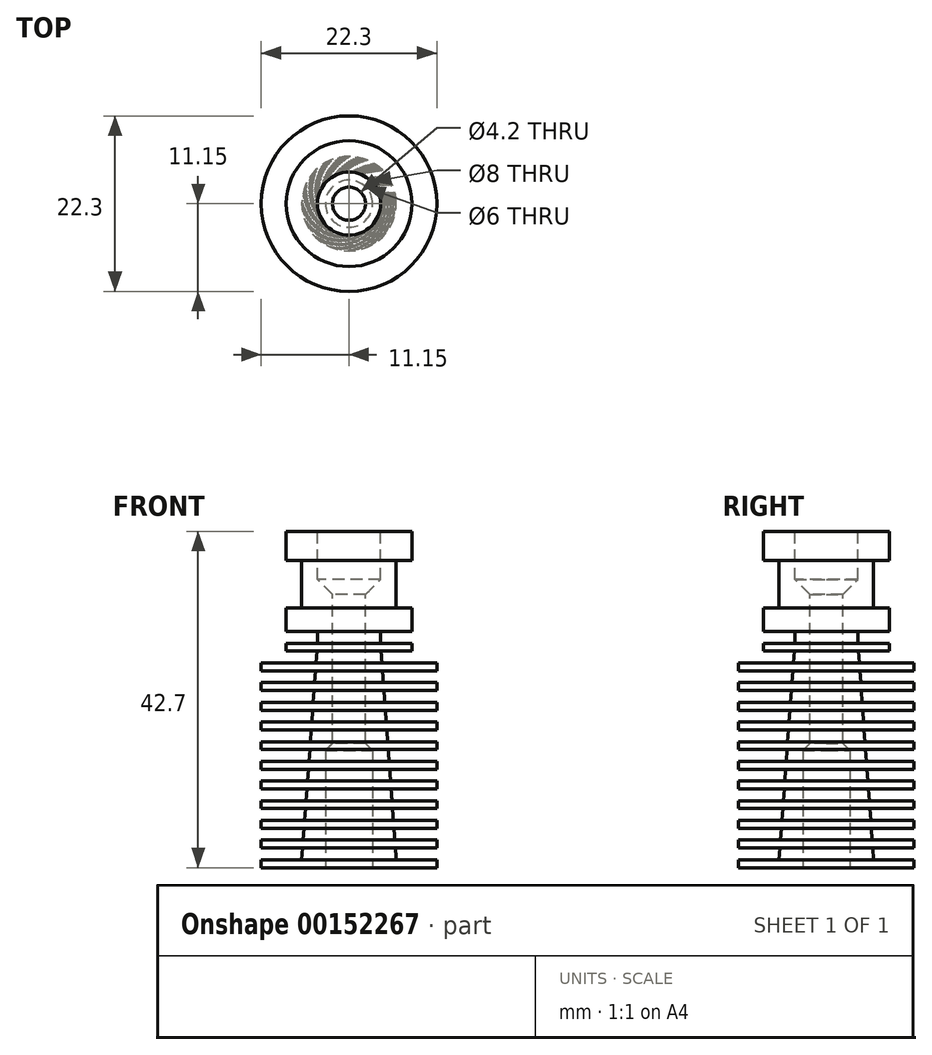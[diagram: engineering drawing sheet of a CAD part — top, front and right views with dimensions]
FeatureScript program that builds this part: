
annotation { "Feature Type Name" : "Feature", "Feature Type Description" : "" }
export const myFeature = defineFeature(function(context is Context, id is Id, definition is map)
    precondition{}
    {
        {
            var Q0;
            Q0=qCreatedBy(makeId("Top.planeOp"),FACE);
            var sketch = newSketch(context, id + "F0", { "sketchPlane" : qUnion([Q0])});
            skCircle(sketch, "E0", {"center": v(0, 0) * mm, "radius": 8 * mm});
            skSolve(sketch);
        }
        {
            var Q0;
            Q0=makeQuery(id+"F0.imprint","IMPRINT",FACE,{"disambiguationData":[TD([[makeQuery(id+"F0.imprint","IMPRINT",EDGE,{"derivedFrom":sQuery(id+"F0.wireOp",EDGE,"E0")}),1.0]])]});
            var Q1;
            Q1=sQuery(id+"F0.wireOp",EDGE,"E0");
            extrude(context, id + "F1", {"entities" : qUnion([Q0]), "surfaceEntities" : qUnion([Q1]), "oppositeDirection" : true, "depth" : 3.7 * mm});
        }
        {
            var Q0;
            Q0=makeQuery(id+"F1.opExtrude","CAP_FACE",FACE,{"disambiguationData":[OSD([sQuery(id+"F0.wireOp",EDGE,"E0")])],"isStart":false});
            var sketch = newSketch(context, id + "F2", { "sketchPlane" : qUnion([Q0])});
            skCircle(sketch, "E1", {"center": v(0, 0) * mm, "radius": 6 * mm});
            skSolve(sketch);
        }
        {
            var Q0;
            Q0=makeQuery(id+"F2.imprint","IMPRINT",FACE,{"disambiguationData":[TD([[makeQuery(id+"F2.imprint","IMPRINT",EDGE,{"derivedFrom":sQuery(id+"F2.wireOp",EDGE,"E1")}),1.0]])]});
            var Q1;
            Q1=sQuery(id+"F2.wireOp",EDGE,"E1");
            extrude(context, id + "F3", {"entities" : qUnion([Q0]), "operationType" : NewBodyOperationType.ADD, "surfaceEntities" : qUnion([Q1]), "depth" : 6 * mm});
        }
        {
            var Q0;
            Q0=makeQuery(id+"F3.opExtrude","CAP_FACE",FACE,{"disambiguationData":[OSD([sQuery(id+"F2.wireOp",EDGE,"E1")])],"isStart":false});
            var sketch = newSketch(context, id + "F4", { "sketchPlane" : qUnion([Q0])});
            skCircle(sketch, "E2", {"center": v(0, 0) * mm, "radius": 8 * mm});
            skSolve(sketch);
        }
        {
            var Q0;
            Q0 = qSketchRegion(id + "F4", true);
            extrude(context, id + "F5", {"entities" : qUnion([Q0]), "operationType" : NewBodyOperationType.ADD, "depth" : 3 * mm});
        }
        {
            var Q0;
            Q0=qCreatedBy(makeId("Front.planeOp"),FACE);
            var sketch = newSketch(context, id + "F6", { "sketchPlane" : qUnion([Q0])});
            skLineSegment(sketch, "E3", {"start": v(0, 0) * mm, "end": v(0, -12.7) * mm});
            skLineSegment(sketch, "E4.bottom", {"start": v(0, -12.7) * mm, "end": v(4, -12.7) * mm});
            skLineSegment(sketch, "E4.top", {"start": v(0, -14.2) * mm, "end": v(4, -14.2) * mm});
            skLineSegment(sketch, "E4.left", {"start": v(0, -12.7) * mm, "end": v(0, -14.2) * mm});
            skLineSegment(sketch, "E4.right", {"start": v(4, -12.7) * mm, "end": v(4, -14.2) * mm});
            skLineSegment(sketch, "E5.bottom", {"start": v(0, -14.2) * mm, "end": v(8, -14.2) * mm});
            skLineSegment(sketch, "E5.top", {"start": v(0, -15.2) * mm, "end": v(8, -15.2) * mm});
            skLineSegment(sketch, "E5.left", {"start": v(0, -14.2) * mm, "end": v(0, -15.2) * mm});
            skLineSegment(sketch, "E5.right", {"start": v(8, -14.2) * mm, "end": v(8, -15.2) * mm});
            skLineSegment(sketch, "E6", {"start": v(0, -15.2) * mm, "end": v(0, -16.7) * mm});
            skLineSegment(sketch, "E7.bottom", {"start": v(0, -16.7) * mm, "end": v(11.15, -16.7) * mm});
            skLineSegment(sketch, "E7.top", {"start": v(0, -17.7) * mm, "end": v(11.15, -17.7) * mm});
            skLineSegment(sketch, "E7.left", {"start": v(0, -16.7) * mm, "end": v(0, -17.7) * mm});
            skLineSegment(sketch, "E7.right", {"start": v(11.15, -16.7) * mm, "end": v(11.15, -17.7) * mm});
            skLineSegment(sketch, "E8.1.0.0", {"start": v(0, -20.2) * mm, "end": v(11.15, -20.2) * mm});
            skLineSegment(sketch, "E8.1.0.1", {"start": v(0, -19.2) * mm, "end": v(11.15, -19.2) * mm});
            skLineSegment(sketch, "E8.1.0.2", {"start": v(0, -19.2) * mm, "end": v(0, -20.2) * mm});
            skLineSegment(sketch, "E8.1.0.3", {"start": v(11.15, -19.2) * mm, "end": v(11.15, -20.2) * mm});
            skLineSegment(sketch, "E8.2.0.0", {"start": v(0, -22.7) * mm, "end": v(11.15, -22.7) * mm});
            skLineSegment(sketch, "E8.2.0.1", {"start": v(0, -21.7) * mm, "end": v(11.15, -21.7) * mm});
            skLineSegment(sketch, "E8.2.0.2", {"start": v(0, -21.7) * mm, "end": v(0, -22.7) * mm});
            skLineSegment(sketch, "E8.2.0.3", {"start": v(11.15, -21.7) * mm, "end": v(11.15, -22.7) * mm});
            skLineSegment(sketch, "E8.3.0.0", {"start": v(0, -25.2) * mm, "end": v(11.15, -25.2) * mm});
            skLineSegment(sketch, "E8.3.0.1", {"start": v(0, -24.2) * mm, "end": v(11.15, -24.2) * mm});
            skLineSegment(sketch, "E8.3.0.2", {"start": v(0, -24.2) * mm, "end": v(0, -25.2) * mm});
            skLineSegment(sketch, "E8.3.0.3", {"start": v(11.15, -24.2) * mm, "end": v(11.15, -25.2) * mm});
            skLineSegment(sketch, "E8.4.0.0", {"start": v(0, -27.7) * mm, "end": v(11.15, -27.7) * mm});
            skLineSegment(sketch, "E8.4.0.1", {"start": v(0, -26.7) * mm, "end": v(11.15, -26.7) * mm});
            skLineSegment(sketch, "E8.4.0.2", {"start": v(0, -26.7) * mm, "end": v(0, -27.7) * mm});
            skLineSegment(sketch, "E8.4.0.3", {"start": v(11.15, -26.7) * mm, "end": v(11.15, -27.7) * mm});
            skLineSegment(sketch, "E8.5.0.0", {"start": v(0, -30.2) * mm, "end": v(11.15, -30.2) * mm});
            skLineSegment(sketch, "E8.5.0.1", {"start": v(0, -29.2) * mm, "end": v(11.15, -29.2) * mm});
            skLineSegment(sketch, "E8.5.0.2", {"start": v(0, -29.2) * mm, "end": v(0, -30.2) * mm});
            skLineSegment(sketch, "E8.5.0.3", {"start": v(11.15, -29.2) * mm, "end": v(11.15, -30.2) * mm});
            skLineSegment(sketch, "E8.6.0.0", {"start": v(0, -32.7) * mm, "end": v(11.15, -32.7) * mm});
            skLineSegment(sketch, "E8.6.0.1", {"start": v(0, -31.7) * mm, "end": v(11.15, -31.7) * mm});
            skLineSegment(sketch, "E8.6.0.2", {"start": v(0, -31.7) * mm, "end": v(0, -32.7) * mm});
            skLineSegment(sketch, "E8.6.0.3", {"start": v(11.15, -31.7) * mm, "end": v(11.15, -32.7) * mm});
            skLineSegment(sketch, "E8.7.0.0", {"start": v(0, -35.2) * mm, "end": v(11.15, -35.2) * mm});
            skLineSegment(sketch, "E8.7.0.1", {"start": v(0, -34.2) * mm, "end": v(11.15, -34.2) * mm});
            skLineSegment(sketch, "E8.7.0.2", {"start": v(0, -34.2) * mm, "end": v(0, -35.2) * mm});
            skLineSegment(sketch, "E8.7.0.3", {"start": v(11.15, -34.2) * mm, "end": v(11.15, -35.2) * mm});
            skLineSegment(sketch, "E8.8.0.0", {"start": v(0, -37.7) * mm, "end": v(11.15, -37.7) * mm});
            skLineSegment(sketch, "E8.8.0.1", {"start": v(0, -36.7) * mm, "end": v(11.15, -36.7) * mm});
            skLineSegment(sketch, "E8.8.0.2", {"start": v(0, -36.7) * mm, "end": v(0, -37.7) * mm});
            skLineSegment(sketch, "E8.8.0.3", {"start": v(11.15, -36.7) * mm, "end": v(11.15, -37.7) * mm});
            skLineSegment(sketch, "E8.9.0.0", {"start": v(0, -40.2) * mm, "end": v(11.15, -40.2) * mm});
            skLineSegment(sketch, "E8.9.0.1", {"start": v(0, -39.2) * mm, "end": v(11.15, -39.2) * mm});
            skLineSegment(sketch, "E8.9.0.2", {"start": v(0, -39.2) * mm, "end": v(0, -40.2) * mm});
            skLineSegment(sketch, "E8.9.0.3", {"start": v(11.15, -39.2) * mm, "end": v(11.15, -40.2) * mm});
            skLineSegment(sketch, "E8.10.0.0", {"start": v(0, -42.7) * mm, "end": v(11.15, -42.7) * mm});
            skLineSegment(sketch, "E8.10.0.1", {"start": v(0, -41.7) * mm, "end": v(11.15, -41.7) * mm});
            skLineSegment(sketch, "E8.10.0.2", {"start": v(0, -41.7) * mm, "end": v(0, -42.7) * mm});
            skLineSegment(sketch, "E8.10.0.3", {"start": v(11.15, -41.7) * mm, "end": v(11.15, -42.7) * mm});
            skLineSegment(sketch, "E8.direction1", {"start": v(0, -17.7) * mm, "end": v(0, -20.2) * mm, "construction": true});
            skLineSegment(sketch, "E9", {"start": v(0, -41.7) * mm, "end": v(6, -41.7) * mm});
            skLineSegment(sketch, "E10", {"start": v(4.07, -15.2) * mm, "end": v(4.18, -16.7) * mm});
            skLineSegment(sketch, "E11.trimOffspring", {"start": v(4.25, -17.7) * mm, "end": v(4.36, -19.2) * mm});
            skLineSegment(sketch, "E12.trimOffspring", {"start": v(4.44, -20.2) * mm, "end": v(4.55, -21.7) * mm});
            skLineSegment(sketch, "E13.trimOffspring", {"start": v(4.62, -22.7) * mm, "end": v(4.73, -24.2) * mm});
            skLineSegment(sketch, "E14.trimOffspring", {"start": v(4.8, -25.2) * mm, "end": v(4.9, -26.7) * mm});
            skLineSegment(sketch, "E15.trimOffspring", {"start": v(4.98, -27.7) * mm, "end": v(5.1, -29.2) * mm});
            skLineSegment(sketch, "E16.trimOffspring", {"start": v(5.16, -30.2) * mm, "end": v(5.27, -31.7) * mm});
            skLineSegment(sketch, "E17.trimOffspring", {"start": v(5.35, -32.7) * mm, "end": v(5.45, -34.2) * mm});
            skLineSegment(sketch, "E18.trimOffspring", {"start": v(5.53, -35.2) * mm, "end": v(5.64, -36.7) * mm});
            skLineSegment(sketch, "E19.trimOffspring", {"start": v(5.7, -37.7) * mm, "end": v(5.82, -39.2) * mm});
            skLineSegment(sketch, "E20.trimOffspring", {"start": v(5.9, -40.2) * mm, "end": v(6, -41.7) * mm});
            skLineSegment(sketch, "E21", {"start": v(0, -17.7) * mm, "end": v(0, -19.2) * mm});
            skLineSegment(sketch, "E22", {"start": v(0, -20.2) * mm, "end": v(0, -21.7) * mm});
            skLineSegment(sketch, "E23", {"start": v(0, -22.7) * mm, "end": v(0, -24.2) * mm});
            skLineSegment(sketch, "E24", {"start": v(0, -25.2) * mm, "end": v(0, -26.7) * mm});
            skLineSegment(sketch, "E25", {"start": v(0, -27.7) * mm, "end": v(0, -29.2) * mm});
            skLineSegment(sketch, "E26", {"start": v(0, -30.2) * mm, "end": v(0, -31.7) * mm});
            skLineSegment(sketch, "E27", {"start": v(0, -32.7) * mm, "end": v(0, -34.2) * mm});
            skLineSegment(sketch, "E28", {"start": v(0, -35.2) * mm, "end": v(0, -36.7) * mm});
            skLineSegment(sketch, "E29", {"start": v(0, -37.7) * mm, "end": v(0, -39.2) * mm});
            skLineSegment(sketch, "E30", {"start": v(0, -40.2) * mm, "end": v(0, -41.7) * mm});
            skSolve(sketch);
        }
        {
            var Q0;
            Q0 = qSketchRegion(id + "F6", true);
            var Q1;
            Q1=sQuery(id+"F6.wireOp",EDGE,"E3");
            revolve(context, id + "F7", {"operationType" : NewBodyOperationType.ADD, "entities" : qUnion([Q0]), "axis" : qUnion([Q1]), "revolveType" : RevolveType.FULL});
        }
        {
            var Q0;
            Q0=makeQuery(id+"F1.opExtrude","CAP_FACE",FACE,{"disambiguationData":[OSD([sQuery(id+"F0.wireOp",EDGE,"E0")])],"isStart":true});
            var sketch = newSketch(context, id + "F8", { "sketchPlane" : qUnion([Q0])});
            skCircle(sketch, "E31", {"center": v(0, 0) * mm, "radius": 2.1 * mm});
            skSolve(sketch);
        }
        {
            var Q0;
            Q0 = qSketchRegion(id + "F8", true);
            extrude(context, id + "F9", {"entities" : qUnion([Q0]), "operationType" : NewBodyOperationType.REMOVE, "oppositeDirection" : true, "depth" : 42.7 * mm});
        }
        {
            var Q0;
            Q0=makeQuery(id+"F1.opExtrude","CAP_FACE",FACE,{"disambiguationData":[OSD([sQuery(id+"F0.wireOp",EDGE,"E0")])],"isStart":true});
            var sketch = newSketch(context, id + "F10", { "sketchPlane" : qUnion([Q0])});
            skCircle(sketch, "E32", {"center": v(0, 0) * mm, "radius": 4 * mm});
            skSolve(sketch);
        }
        {
            var Q0;
            Q0 = qSketchRegion(id + "F10", true);
            extrude(context, id + "F11", {"entities" : qUnion([Q0]), "operationType" : NewBodyOperationType.REMOVE, "oppositeDirection" : true, "depth" : 6 * mm});
        }
        {
            var Q0;
            Q0=makeQuery(id+"F11.boolean.opBoolean","INTERSECT",EDGE,{"derivedFrom":[makeQuery(id+"F9.boolean.opBoolean","COPY",FACE,{"derivedFrom":makeQuery(id+"F9.opExtrude","SWEPT_FACE",FACE,{"disambiguationData":[OSD([sQuery(id+"F8.wireOp",EDGE,"E31")])]})}),makeQuery(id+"F11.opExtrude","CAP_FACE",FACE,{"disambiguationData":[OSD([sQuery(id+"F10.wireOp",EDGE,"E32")])],"isStart":false})]});
            chamfer(context, id + "F12", {"entities" : qUnion([Q0]), "width" : 2 * mm, "tangentPropagation" : true});
        }
        {
            var Q0;
            Q0=makeQuery(id+"F7.opRevolve","SWEPT_FACE",FACE,{"disambiguationData":[OSD([sQuery(id+"F6.wireOp",EDGE,"E8.10.0.0")])]});
            var sketch = newSketch(context, id + "F13", { "sketchPlane" : qUnion([Q0])});
            skCircle(sketch, "E33", {"center": v(0, 0) * mm, "radius": 3 * mm});
            skSolve(sketch);
        }
        {
            var Q0;
            Q0 = qSketchRegion(id + "F13", true);
            extrude(context, id + "F14", {"entities" : qUnion([Q0]), "operationType" : NewBodyOperationType.REMOVE, "oppositeDirection" : true, "depth" : 14.8 * mm});
        }
        {
            var Q0;
            Q0=makeQuery(id+"F14.boolean.opBoolean","INTERSECT",EDGE,{"derivedFrom":[makeQuery(id+"F9.boolean.opBoolean","COPY",FACE,{"derivedFrom":makeQuery(id+"F9.opExtrude","SWEPT_FACE",FACE,{"disambiguationData":[OSD([sQuery(id+"F8.wireOp",EDGE,"E31")])]})}),makeQuery(id+"F14.opExtrude","CAP_FACE",FACE,{"disambiguationData":[OSD([sQuery(id+"F13.wireOp",EDGE,"E33")])],"isStart":false})]});
            chamfer(context, id + "F15", {"entities" : qUnion([Q0]), "width" : 1 * mm, "tangentPropagation" : true});
        }
    });
